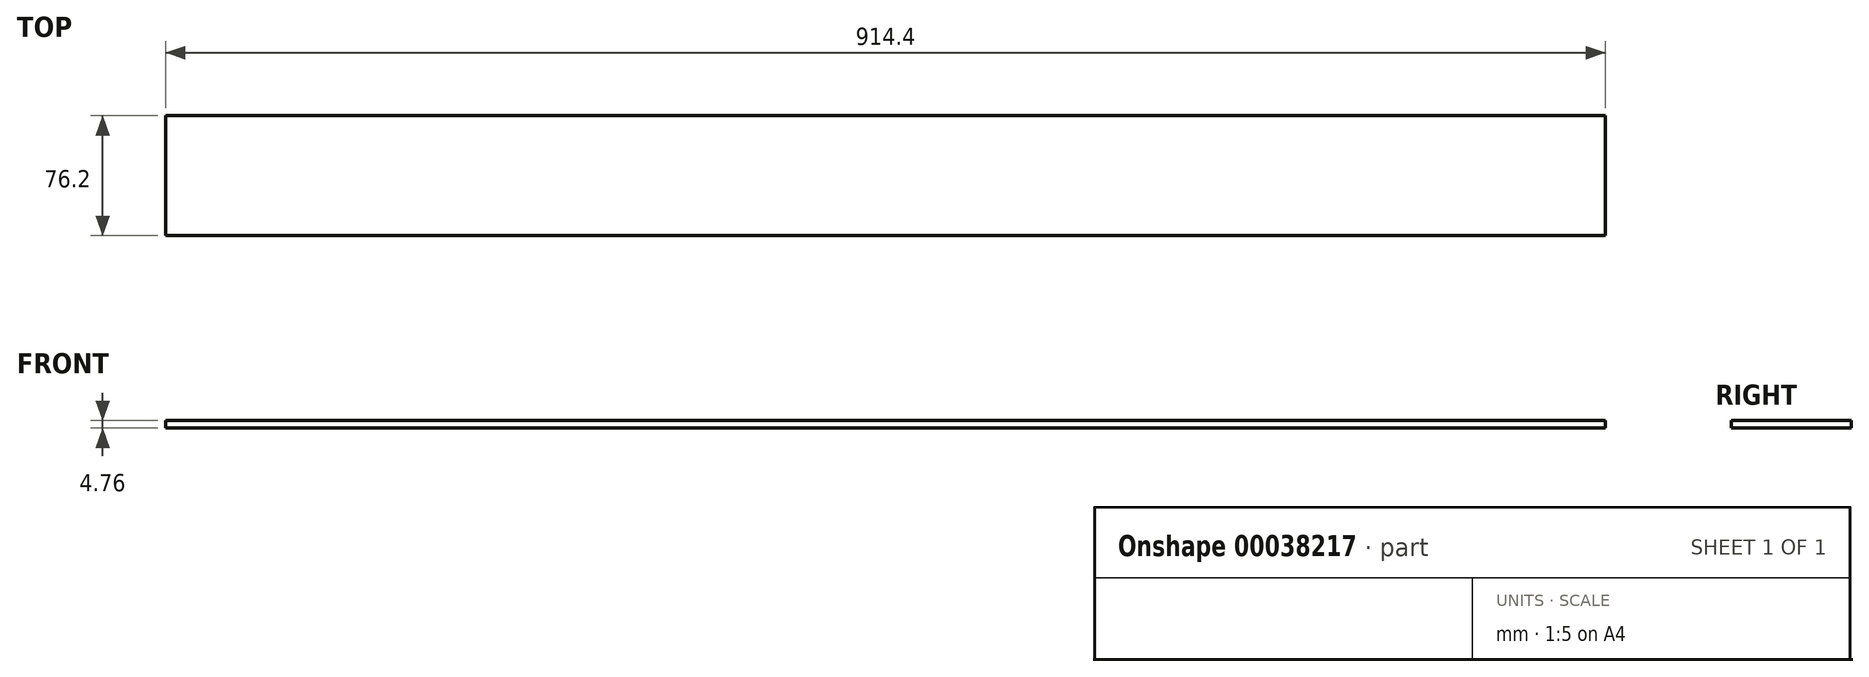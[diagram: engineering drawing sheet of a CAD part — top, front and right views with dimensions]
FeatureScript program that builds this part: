
annotation { "Feature Type Name" : "Feature", "Feature Type Description" : "" }
export const myFeature = defineFeature(function(context is Context, id is Id, definition is map)
    precondition{}
    {
        {
            var Q0;
            Q0=qCreatedBy(makeId("Top.planeOp"),FACE);
            var sketch = newSketch(context, id + "F0", { "sketchPlane" : qUnion([Q0])});
            skLineSegment(sketch, "E0.rect.bottom", {"start": v(457.2, -38.1) * mm, "end": v(-457.2, -38.1) * mm});
            skLineSegment(sketch, "E0.rect.top", {"start": v(457.2, 38.1) * mm, "end": v(-457.2, 38.1) * mm});
            skLineSegment(sketch, "E0.rect.left", {"start": v(457.2, -38.1) * mm, "end": v(457.2, 38.1) * mm});
            skLineSegment(sketch, "E0.rect.right", {"start": v(-457.2, -38.1) * mm, "end": v(-457.2, 38.1) * mm});
            skPoint(sketch, "E0.rect.middle", {"position": v(0, 0) * mm});
            skSolve(sketch);
        }
        {
            var Q0;
            Q0 = qSketchRegion(id + "F0", true);
            extrude(context, id + "F1", {"entities" : qUnion([Q0]), "oppositeDirection" : true, "depth" : 4.76 * mm});
        }
    });
